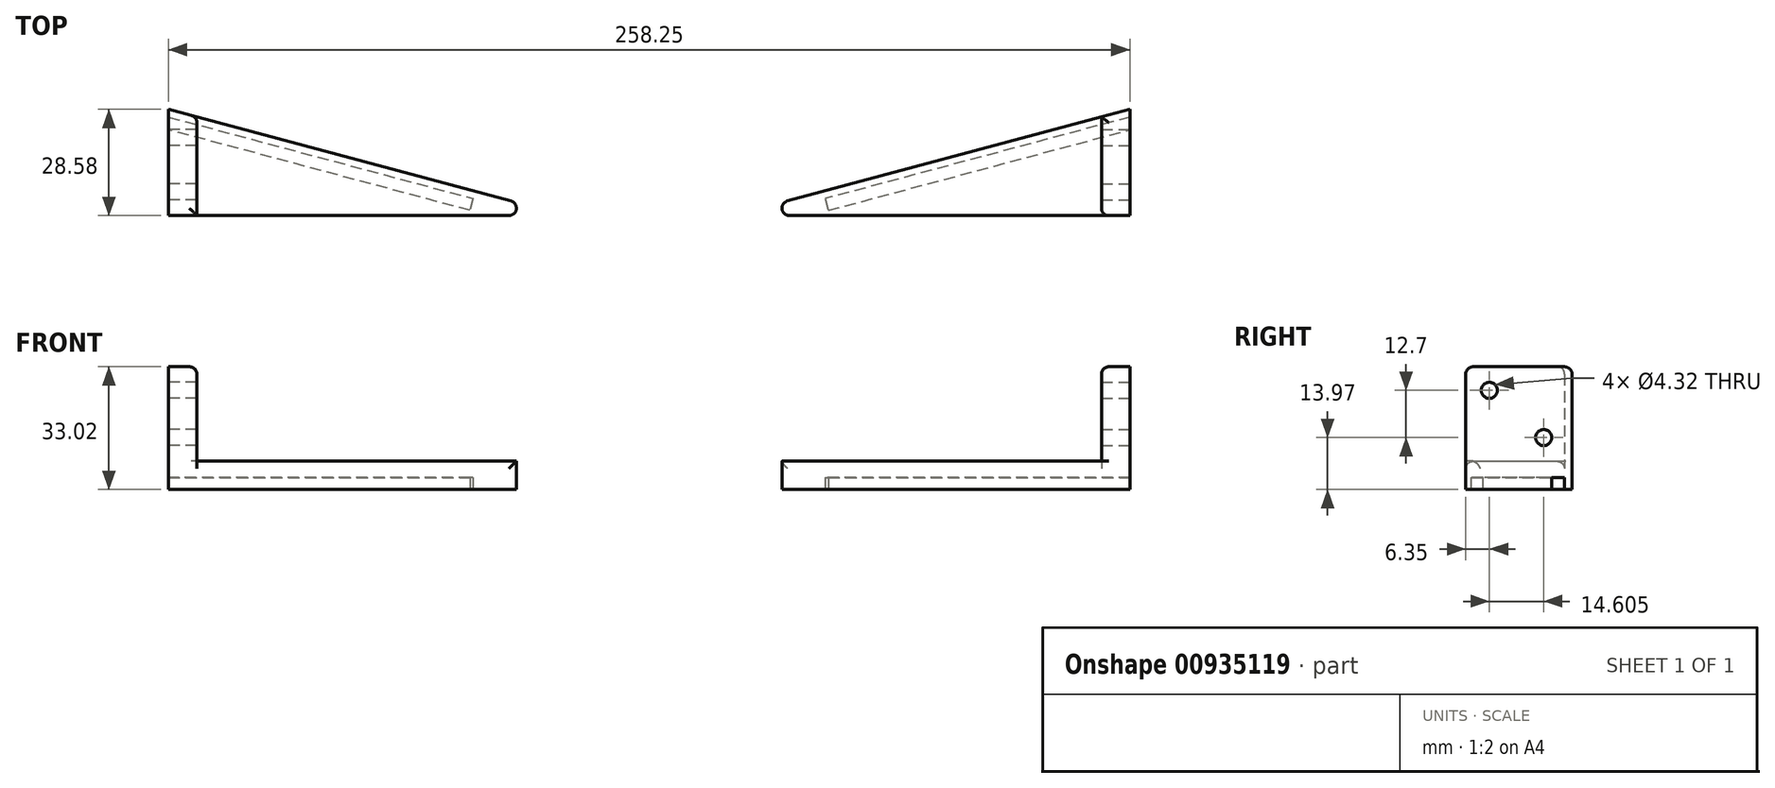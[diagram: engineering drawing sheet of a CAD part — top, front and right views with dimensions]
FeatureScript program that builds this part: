
annotation { "Feature Type Name" : "Feature", "Feature Type Description" : "" }
export const myFeature = defineFeature(function(context is Context, id is Id, definition is map)
    precondition{}
    {
        {
            var Q0;
            Q0=qCreatedBy(makeId("Top.planeOp"),FACE);
            var sketch = newSketch(context, id + "F0", { "sketchPlane" : qUnion([Q0])});
            skLineSegment(sketch, "E0", {"start": v(20.22, 0) * mm, "end": v(126.86, 28.58) * mm});
            skLineSegment(sketch, "E1", {"start": v(126.86, 28.58) * mm, "end": v(126.86, 0) * mm});
            skLineSegment(sketch, "E2", {"start": v(126.86, 0) * mm, "end": v(20.22, 0) * mm});
            skSolve(sketch);
        }
        {
            var Q0;
            Q0=qCreatedBy(makeId("Top.planeOp"),FACE);
            var sketch = newSketch(context, id + "F1", { "sketchPlane" : qUnion([Q0])});
            skLineSegment(sketch, "E3", {"start": v(-24.75, 0) * mm, "end": v(-131.4, 28.58) * mm});
            skLineSegment(sketch, "E4", {"start": v(-131.4, 28.58) * mm, "end": v(-131.4, 0) * mm});
            skLineSegment(sketch, "E5", {"start": v(-131.4, 0) * mm, "end": v(-24.75, 0) * mm});
            skSolve(sketch);
        }
        {
            var Q0;
            Q0=makeQuery(id+"F0.imprint","IMPRINT",FACE,{"disambiguationData":[TD([[makeQuery(id+"F0.imprint","IMPRINT",EDGE,{"derivedFrom":sQuery(id+"F0.wireOp",EDGE,"E0")}),-1.0]])]});
            extrude(context, id + "F2", {"entities" : qUnion([Q0]), "offsetDistance" : 25.4 * mm, "depth" : 7.62 * mm});
        }
        {
            var Q0;
            Q0=makeQuery(id+"F1.imprint","IMPRINT",FACE,{"disambiguationData":[TD([[makeQuery(id+"F1.imprint","IMPRINT",EDGE,{"derivedFrom":sQuery(id+"F1.wireOp",EDGE,"E3")}),1.0]])]});
            extrude(context, id + "F3", {"entities" : qUnion([Q0]), "offsetDistance" : 25.4 * mm, "depth" : 7.62 * mm});
        }
        {
            var Q0;
            Q0=makeQuery(id+"F2.opExtrude","CAP_FACE",FACE,{"disambiguationData":[OSD([sQuery(id+"F0.wireOp",EDGE,"E0"),sQuery(id+"F0.wireOp",EDGE,"E1"),sQuery(id+"F0.wireOp",EDGE,"E2")])],"isStart":false});
            var sketch = newSketch(context, id + "F4", { "sketchPlane" : qUnion([Q0])});
            skLineSegment(sketch, "E6", {"start": v(119.24, 26.53) * mm, "end": v(126.86, 28.58) * mm});
            skLineSegment(sketch, "E7", {"start": v(126.86, 28.58) * mm, "end": v(126.86, 0) * mm});
            skLineSegment(sketch, "E8", {"start": v(126.86, 0) * mm, "end": v(119.24, 0) * mm});
            skLineSegment(sketch, "E9", {"start": v(119.24, 0) * mm, "end": v(119.24, 26.53) * mm});
            skSolve(sketch);
        }
        {
            var Q0;
            Q0=makeQuery(id+"F4.imprint","IMPRINT",FACE,{"disambiguationData":[TD([[makeQuery(id+"F4.imprint","IMPRINT",EDGE,{"derivedFrom":sQuery(id+"F4.wireOp",EDGE,"E6")}),-1.0]])]});
            extrude(context, id + "F5", {"entities" : qUnion([Q0]), "operationType" : NewBodyOperationType.ADD, "offsetDistance" : 25.4 * mm, "depth" : 25.4 * mm});
        }
        {
            var Q0;
            Q0=makeQuery(id+"F3.opExtrude","CAP_FACE",FACE,{"disambiguationData":[OSD([sQuery(id+"F1.wireOp",EDGE,"E3"),sQuery(id+"F1.wireOp",EDGE,"E4"),sQuery(id+"F1.wireOp",EDGE,"E5")])],"isStart":false});
            var sketch = newSketch(context, id + "F6", { "sketchPlane" : qUnion([Q0])});
            skLineSegment(sketch, "E10", {"start": v(-131.4, 0) * mm, "end": v(-123.77, 0) * mm});
            skLineSegment(sketch, "E11", {"start": v(-123.77, 0) * mm, "end": v(-123.77, 26.53) * mm});
            skLineSegment(sketch, "E12", {"start": v(-123.77, 26.53) * mm, "end": v(-131.4, 28.58) * mm});
            skLineSegment(sketch, "E13", {"start": v(-131.4, 28.58) * mm, "end": v(-131.4, 0) * mm});
            skSolve(sketch);
        }
        {
            var Q0;
            Q0=makeQuery(id+"F6.imprint","IMPRINT",FACE,{"disambiguationData":[TD([[makeQuery(id+"F6.imprint","IMPRINT",EDGE,{"derivedFrom":sQuery(id+"F6.wireOp",EDGE,"E10")}),1.0]])]});
            extrude(context, id + "F7", {"entities" : qUnion([Q0]), "operationType" : NewBodyOperationType.ADD, "offsetDistance" : 25.4 * mm, "depth" : 25.4 * mm});
        }
        {
            var Q0;
            Q0=makeQuery(id+"F2.opExtrude","CAP_FACE",FACE,{"disambiguationData":[OSD([sQuery(id+"F0.wireOp",EDGE,"E0"),sQuery(id+"F0.wireOp",EDGE,"E1"),sQuery(id+"F0.wireOp",EDGE,"E2")])],"isStart":true});
            var sketch = newSketch(context, id + "F8", { "sketchPlane" : qUnion([Q0])});
            skLineSegment(sketch, "E14", {"start": v(126.86, -26.5) * mm, "end": v(45.04, -4.58) * mm});
            skLineSegment(sketch, "E15", {"start": v(45.04, -4.58) * mm, "end": v(45.9, -1.4) * mm});
            skLineSegment(sketch, "E16", {"start": v(45.9, -1.4) * mm, "end": v(126.86, -23.09) * mm});
            skLineSegment(sketch, "E17", {"start": v(126.86, -23.09) * mm, "end": v(126.86, -26.5) * mm});
            skSolve(sketch);
        }
        {
            var Q0;
            Q0=makeQuery(id+"F8.imprint","IMPRINT",FACE,{"disambiguationData":[TD([[makeQuery(id+"F8.imprint","IMPRINT",EDGE,{"derivedFrom":sQuery(id+"F8.wireOp",EDGE,"E14")}),-1.0]])]});
            extrude(context, id + "F9", {"entities" : qUnion([Q0]), "operationType" : NewBodyOperationType.REMOVE, "oppositeDirection" : true, "offsetDistance" : 25.4 * mm, "depth" : 3.17 * mm});
        }
        {
            var Q0;
            Q0=makeQuery(id+"F3.opExtrude","CAP_FACE",FACE,{"disambiguationData":[OSD([sQuery(id+"F1.wireOp",EDGE,"E3"),sQuery(id+"F1.wireOp",EDGE,"E4"),sQuery(id+"F1.wireOp",EDGE,"E5")])],"isStart":true});
            var sketch = newSketch(context, id + "F10", { "sketchPlane" : qUnion([Q0])});
            skLineSegment(sketch, "E18", {"start": v(-131.4, -26.5) * mm, "end": v(-49.57, -4.58) * mm});
            skLineSegment(sketch, "E19", {"start": v(-49.57, -4.58) * mm, "end": v(-50.43, -1.4) * mm});
            skLineSegment(sketch, "E20", {"start": v(-50.43, -1.4) * mm, "end": v(-131.4, -23.09) * mm});
            skLineSegment(sketch, "E21", {"start": v(-131.4, -23.09) * mm, "end": v(-131.4, -26.5) * mm});
            skSolve(sketch);
        }
        {
            var Q0;
            Q0=makeQuery(id+"F10.imprint","IMPRINT",FACE,{"disambiguationData":[TD([[makeQuery(id+"F10.imprint","IMPRINT",EDGE,{"derivedFrom":sQuery(id+"F10.wireOp",EDGE,"E18")}),1.0]])]});
            extrude(context, id + "F11", {"entities" : qUnion([Q0]), "operationType" : NewBodyOperationType.REMOVE, "oppositeDirection" : true, "offsetDistance" : 25.4 * mm, "depth" : 3.17 * mm});
        }
        {
            var Q0;
            Q0=makeQuery(id+"F7.opExtrude","CAP_EDGE",EDGE,{"disambiguationData":[OSD([sQuery(id+"F6.wireOp",EDGE,"E11")])],"isStart":true});
            var Q1;
            Q1=makeQuery(id+"F7.opExtrude","SWEPT_EDGE",EDGE,{"disambiguationData":[OSD([sQuery(id+"F1.wireOp",EDGE,"E3"),sQuery(id+"F6.wireOp",EDGE,"E11"),sQuery(id+"F6.wireOp",EDGE,"E12")])]});
            var Q2;
            Q2=makeQuery(id+"F3.opExtrude","CAP_EDGE",EDGE,{"disambiguationData":[OSD([sQuery(id+"F1.wireOp",EDGE,"E5")])],"isStart":false});
            var Q3;
            Q3=makeQuery(id+"F3.opExtrude","SWEPT_EDGE",EDGE,{"disambiguationData":[OSD([sQuery(id+"F1.wireOp",EDGE,"E3"),sQuery(id+"F1.wireOp",EDGE,"E5")])]});
            var Q4;
            Q4=makeQuery(id+"F7.opExtrude","CAP_EDGE",EDGE,{"disambiguationData":[OSD([sQuery(id+"F6.wireOp",EDGE,"E12")])],"isStart":false});
            var Q5;
            Q5=makeQuery(id+"F7.opExtrude","CAP_EDGE",EDGE,{"disambiguationData":[OSD([sQuery(id+"F6.wireOp",EDGE,"E11")])],"isStart":false});
            var Q6;
            Q6=makeQuery(id+"F7.opExtrude","CAP_EDGE",EDGE,{"disambiguationData":[OSD([sQuery(id+"F6.wireOp",EDGE,"E10")])],"isStart":false});
            fillet(context, id + "F12", {"entities" : qUnion([Q0, Q1, Q2, Q3, Q4, Q5, Q6]), "radius" : 2 * mm, "tangentPropagation" : true, "allowEdgeOverflow" : false});
        }
        {
            var Q0;
            Q0=makeQuery(id+"F5.opExtrude","CAP_EDGE",EDGE,{"disambiguationData":[OSD([sQuery(id+"F4.wireOp",EDGE,"E9")])],"isStart":true});
            var Q1;
            Q1=makeQuery(id+"F2.opExtrude","CAP_EDGE",EDGE,{"disambiguationData":[OSD([sQuery(id+"F0.wireOp",EDGE,"E0")])],"isStart":false});
            var Q2;
            Q2=makeQuery(id+"F5.opExtrude","CAP_EDGE",EDGE,{"disambiguationData":[OSD([sQuery(id+"F4.wireOp",EDGE,"E9")])],"isStart":false});
            var Q3;
            Q3=makeQuery(id+"F5.opExtrude","CAP_EDGE",EDGE,{"disambiguationData":[OSD([sQuery(id+"F4.wireOp",EDGE,"E6")])],"isStart":false});
            var Q4;
            Q4=makeQuery(id+"F5.opExtrude","CAP_EDGE",EDGE,{"disambiguationData":[OSD([sQuery(id+"F4.wireOp",EDGE,"E8")])],"isStart":false});
            var Q5;
            Q5=makeQuery(id+"F5.opExtrude","SWEPT_EDGE",EDGE,{"disambiguationData":[OSD([sQuery(id+"F0.wireOp",EDGE,"E2"),sQuery(id+"F4.wireOp",EDGE,"E8"),sQuery(id+"F4.wireOp",EDGE,"E9")])]});
            var Q6;
            Q6=makeQuery(id+"F2.opExtrude","SWEPT_EDGE",EDGE,{"disambiguationData":[OSD([sQuery(id+"F0.wireOp",EDGE,"E0"),sQuery(id+"F0.wireOp",EDGE,"E2")])]});
            fillet(context, id + "F13", {"entities" : qUnion([Q0, Q1, Q2, Q3, Q4, Q5, Q6]), "radius" : 2 * mm, "tangentPropagation" : true, "allowEdgeOverflow" : false});
        }
        {
            var Q0;
            Q0=makeQuery(id+"F5.boolean.opBoolean","MERGE",FACE,{"derivedFrom":[makeQuery(id+"F2.opExtrude","SWEPT_FACE",FACE,{"disambiguationData":[OSD([sQuery(id+"F0.wireOp",EDGE,"E1")])]}),makeQuery(id+"F5.opExtrude","SWEPT_FACE",FACE,{"disambiguationData":[OSD([sQuery(id+"F4.wireOp",EDGE,"E7")])]})]});
            var sketch = newSketch(context, id + "F14", { "sketchPlane" : qUnion([Q0])});
            skCircle(sketch, "E22", {"center": v(6.35, 26.67) * mm, "radius": 2.16 * mm});
            skCircle(sketch, "E23", {"center": v(20.96, 13.97) * mm, "radius": 2.16 * mm});
            skSolve(sketch);
        }
        {
            var Q0;
            Q0=makeQuery(id+"F14.imprint","IMPRINT",FACE,{"disambiguationData":[TD([[makeQuery(id+"F14.imprint","IMPRINT",EDGE,{"derivedFrom":sQuery(id+"F14.wireOp",EDGE,"E22")}),1.0]])]});
            var Q1;
            Q1=makeQuery(id+"F14.imprint","IMPRINT",FACE,{"disambiguationData":[TD([[makeQuery(id+"F14.imprint","IMPRINT",EDGE,{"derivedFrom":sQuery(id+"F14.wireOp",EDGE,"E23")}),1.0]])]});
            var Q2;
            Q2=sQuery(id+"F14.wireOp",EDGE,"E22");
            extrude(context, id + "F15", {"entities" : qUnion([Q0, Q1]), "operationType" : NewBodyOperationType.REMOVE, "surfaceEntities" : qUnion([Q2]), "oppositeDirection" : true, "depth" : 7.62 * mm, "offsetDistance" : 25.4 * mm});
        }
        {
            var Q0;
            Q0=makeQuery(id+"F7.boolean.opBoolean","MERGE",FACE,{"derivedFrom":[makeQuery(id+"F3.opExtrude","SWEPT_FACE",FACE,{"disambiguationData":[OSD([sQuery(id+"F1.wireOp",EDGE,"E4")])]}),makeQuery(id+"F7.opExtrude","SWEPT_FACE",FACE,{"disambiguationData":[OSD([sQuery(id+"F6.wireOp",EDGE,"E13")])]})]});
            var sketch = newSketch(context, id + "F16", { "sketchPlane" : qUnion([Q0])});
            skCircle(sketch, "E24", {"center": v(-20.96, 13.97) * mm, "radius": 2.16 * mm});
            skCircle(sketch, "E25", {"center": v(-6.35, 26.67) * mm, "radius": 2.16 * mm});
            skSolve(sketch);
        }
        {
            var Q0;
            Q0=makeQuery(id+"F16.imprint","IMPRINT",FACE,{"disambiguationData":[TD([[makeQuery(id+"F16.imprint","IMPRINT",EDGE,{"derivedFrom":sQuery(id+"F16.wireOp",EDGE,"E24")}),1.0]])]});
            var Q1;
            Q1=makeQuery(id+"F16.imprint","IMPRINT",FACE,{"disambiguationData":[TD([[makeQuery(id+"F16.imprint","IMPRINT",EDGE,{"derivedFrom":sQuery(id+"F16.wireOp",EDGE,"E25")}),1.0]])]});
            extrude(context, id + "F17", {"entities" : qUnion([Q0, Q1]), "operationType" : NewBodyOperationType.REMOVE, "oppositeDirection" : true, "depth" : 7.62 * mm, "offsetDistance" : 25.4 * mm});
        }
    });
